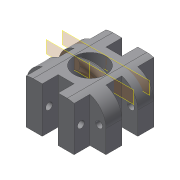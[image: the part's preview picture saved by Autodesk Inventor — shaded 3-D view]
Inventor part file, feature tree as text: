
AUTODESK INVENTOR PART (.ipt)
format: ipt  version: 2018 (Build 220112000, 112)  size: 273,408 bytes
history: native  units: mm
features: sketch x4, extrude x3, plane x2, fillet x2, pattern_circular x1, other x1, helix x1
ambient origin geometry x8: Origin, YZ Plane, XZ Plane, XY Plane, X Axis, Y Axis, Z Axis, Center Point
bodies: Solid1 (feature_tree)
feature tree (14):
  extrude  "Extrusion1"  Depth=20.0mm
  extrude  "Extrusion6"  Depth=7.0mm
  extrude  "Extrusion7"  Depth=7.0mm
  pattern_circular  "Circular Pattern3"  [2 undecoded]
  plane  "Work Plane3"
  sketch  "Sketch10"  dims[d59=7.0mm d60=7.0mm d61=7.0mm d62=90.0deg d63=7.0mm d64=7.0mm d65=90.0deg d66=7.0mm d67=7.0mm d68=7.0mm d69=7.0mm d70=7.0mm d71=7.0mm d72=7.0mm d73=7.0mm d74=7.0mm d75=7.0mm d76=7.0mm d77=90.0deg d78=13.0mm d81=10.0mm d82=0.0mm d83=3.0mm d84=3.0mm d85=10.0mm d86=0.0mm d87=40.0mm d88=360.0deg d93=7.0mm d94=14.0mm d95=7.0mm d100=2.5mm d101=5.0mm d102=25.0mm d103=15.0mm d104=10.0mm d105=0.0mm d106=90.0deg d107=90.0deg d108=0.0mm d109=0.0mm d111=2.0mm d112=10.0mm]
  other  "Work Axis1"
  helix  "Coil1"  [1 undecoded]
  fillet  "Fillet4"  [1 undecoded]
  fillet  "Fillet5"  Radius=7.0mm
  sketch  "Sketch1"  dims[d28=20.0mm d29=0.0mm d49=13.0mm]
  sketch  "Sketch6"  dims[d55=7.0mm d56=7.0mm]
  sketch  "Sketch7"  dims[d57=7.0mm d58=7.0mm]
  plane  "Work Plane2"
note: 4 required parameter values undecoded (feature->parameter linkage not recoverable at this tier; creation-order binding heuristic only, values carry confidence <= 0.55)
